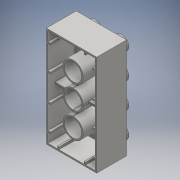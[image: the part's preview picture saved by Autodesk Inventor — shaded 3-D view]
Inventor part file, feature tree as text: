
AUTODESK INVENTOR PART (.ipt)
format: ipt  version: 2016 (Build 200138000, 138)  size: 515,584 bytes
history: native  units: mm
features: sketch x43, extrude x42, projected_geometry x3
ambient origin geometry x8: Origin, YZ Plane, XZ Plane, XY Plane, X Axis, Y Axis, Z Axis, Center Point
bodies: Solid1 (feature_tree)
feature tree (88):
  extrude  "Extrusion1"  Depth=64.0mm
  extrude  "Extrusion2"  Depth=3.0mm
  extrude  "Extrusion3"  Depth=9.0mm
  extrude  "Extrusion4"  Depth=40.0mm
  extrude  "Extrusion5"  Depth=7.0mm
  extrude  "Extrusion6"  Depth=7.0mm
  extrude  "Extrusion7"  Depth=7.0mm
  extrude  "Extrusion8"  Depth=7.0mm
  extrude  "Extrusion9"  Depth=7.0mm
  extrude  "Extrusion10"  Depth=7.0mm
  extrude  "Extrusion11"  Depth=7.0mm
  extrude  "Extrusion12"  Depth=7.0mm
  extrude  "Extrusion13"  Depth=1.0mm
  extrude  "Extrusion14"  Depth=17.0mm
  extrude  "Extrusion15"  Depth=20.0mm
  extrude  "Extrusion16"  Depth=16.0mm
  extrude  "Extrusion17"  Depth=16.0mm TaperAngle=0.0deg
  extrude  "Extrusion18"  Depth=16.0mm TaperAngle=0.0deg
  extrude  "Extrusion19"  Depth=1.0mm
  extrude  "Extrusion20"  Depth=16.0mm TaperAngle=0.0deg
  extrude  "Extrusion21"  Depth=0.5mm
  extrude  "Extrusion22"  Depth=16.0mm TaperAngle=0.0deg
  extrude  "Extrusion23"  Depth=7.0mm
  extrude  "Extrusion24"  Depth=6.0mm
  extrude  "Extrusion25"  Depth=16.0mm TaperAngle=0.0deg
  extrude  "Extrusion26"  Depth=2.5mm TaperAngle=0.0deg
  extrude  "Extrusion27"  Depth=3.5mm TaperAngle=0.0deg
  extrude  "Extrusion28"  Depth=7.0mm
  extrude  "Extrusion29"  Depth=7.0mm
  extrude  "Extrusion30"  Depth=18.0mm TaperAngle=0.0deg
  extrude  "Extrusion31"  Depth=7.0mm
  extrude  "Extrusion32"  Depth=6.0mm
  extrude  "Extrusion33"  Depth=6.0mm
  extrude  "Extrusion34"  Depth=6.0mm
  extrude  "Extrusion35"  Depth=5.5mm
  extrude  "Extrusion36"  Depth=1.0mm
  extrude  "Extrusion37"  Depth=17.0mm TaperAngle=0.0deg
  extrude  "Extrusion38"  Depth=17.0mm TaperAngle=0.0deg
  extrude  "Extrusion39"  Depth=4.5mm
  extrude  "Extrusion40"  Depth=1.0mm
  extrude  "Extrusion41"  Depth=17.0mm TaperAngle=0.0deg
  extrude  "Extrusion42"  Depth=17.0mm TaperAngle=0.0deg
  sketch  "Sketch45"  dims[d143=1.0mm d144=5.5mm d145=17.0mm d146=0.0mm d147=4.5mm d148=17.0mm d149=0.0mm d150=1.0mm d151=0.0mm d152=1.0mm d153=0.0mm d154=1.0mm d155=0.0mm d156=23.0mm d157=1.5mm d158=1.0mm d159=22.0mm d160=1.5mm d161=1.0mm d162=22.0mm d163=1.5mm d164=1.0mm d165=1.5mm d166=1.0mm d167=18.0mm d168=0.0mm d169=1.5mm d170=1.0mm d171=1.5mm d172=1.0mm d173=1.0mm d174=0.0mm]
  sketch  "Sketch1"  dims[d0=32.0mm d1=64.0mm]
  sketch  "Sketch2"  dims[d2=19.0mm d3=0.0mm d4=3.0mm]
  projected_geometry  "Projected Loop1"
  sketch  "Sketch3"  dims[d5=9.0mm d6=9.0mm]
  sketch  "Sketch4"  dims[d7=40.0mm d9=16.3mm d10=10.0mm d12=10.0mm d14=40.0mm d16=16.3mm d17=10.0mm d19=10.0mm]
  sketch  "Sketch5"  dims[d21=4.5mm d22=0.0mm d23=7.0mm]
  sketch  "Sketch6"  dims[d24=4.5mm d25=0.0mm d26=7.0mm]
  sketch  "Sketch7"  dims[d27=4.5mm d28=0.0mm d29=7.0mm]
  sketch  "Sketch8"  dims[d30=4.5mm d31=0.0mm d32=7.0mm]
  sketch  "Sketch9"  dims[d33=4.5mm d34=0.0mm d35=7.0mm]
  sketch  "Sketch10"  dims[d36=4.5mm d37=0.0mm d38=7.0mm]
  sketch  "Sketch11"  dims[d39=4.5mm d40=0.0mm d41=7.0mm]
  projected_geometry  "Projected Loop2"
  sketch  "Sketch12"  dims[d42=4.5mm d43=0.0mm d44=7.0mm]
  projected_geometry  "Projected Loop3"
  sketch  "Sketch13"  dims[d45=4.5mm d46=0.0mm d47=1.0mm]
  sketch  "Sketch14"  dims[d48=17.0mm d49=0.0mm d50=13.0mm]
  sketch  "Sketch15"  dims[d51=20.0mm d53=15.5mm d54=10.0mm d56=10.0mm d58=20.0mm d60=15.5mm d61=10.0mm d63=10.0mm]
  sketch  "Sketch16"  dims[d65=16.0mm d66=0.0mm d67=11.0mm]
  sketch  "Sketch17"  dims[d68=11.0mm d69=16.0mm d70=0.0mm]
  sketch  "Sketch18"  dims[d71=11.0mm d72=16.0mm d73=0.0mm]
  sketch  "Sketch19"  dims[d74=30.0mm d75=1.0mm]
  sketch  "Sketch20"  dims[d76=16.0mm d77=0.0mm d78=16.0mm d79=0.0mm]
  sketch  "Sketch21"  dims[d80=16.0mm d81=0.0mm d82=0.5mm]
  sketch  "Sketch22"  dims[d83=16.0mm d84=0.0mm d85=16.0mm d86=0.0mm]
  sketch  "Sketch23"  dims[d87=7.0mm d88=7.0mm]
  sketch  "Sketch24"  dims[d89=16.0mm d90=0.0mm d91=6.0mm]
  sketch  "Sketch25"  dims[d92=6.0mm d93=16.0mm d94=0.0mm]
  sketch  "Sketch26"  dims[d95=2.5mm d96=0.0mm d97=2.5mm d98=0.0mm]
  sketch  "Sketch27"  dims[d99=3.5mm d100=0.0mm d101=3.5mm d102=0.0mm]
  sketch  "Sketch28"  dims[d103=7.0mm d104=7.0mm]
  sketch  "Sketch29"  dims[d105=18.0mm d106=0.0mm d107=7.0mm]
  sketch  "Sketch30"  dims[d108=7.0mm d109=18.0mm d110=0.0mm]
  sketch  "Sketch31"  dims[d111=7.0mm d112=7.0mm]
  sketch  "Sketch32"  dims[d113=18.0mm d114=0.0mm d115=6.0mm]
  sketch  "Sketch33"  dims[d116=6.0mm d117=6.0mm]
  sketch  "Sketch34"  dims[d118=6.0mm d119=6.0mm]
  sketch  "Sketch35"  dims[d120=18.0mm d121=0.0mm d122=5.5mm]
  sketch  "Sketch36"  dims[d123=17.0mm d124=0.0mm d125=1.0mm]
  sketch  "Sketch37"  dims[d126=4.5mm d127=17.0mm d128=0.0mm]
  sketch  "Sketch40"  dims[d129=5.5mm d130=17.0mm d131=0.0mm]
  sketch  "Sketch41"  dims[d132=1.0mm d133=4.5mm]
  sketch  "Sketch42"  dims[d134=17.0mm d135=0.0mm d136=1.0mm]
  sketch  "Sketch43"  dims[d137=5.5mm d138=17.0mm d139=0.0mm]
  sketch  "Sketch44"  dims[d140=4.5mm d141=17.0mm d142=0.0mm]
